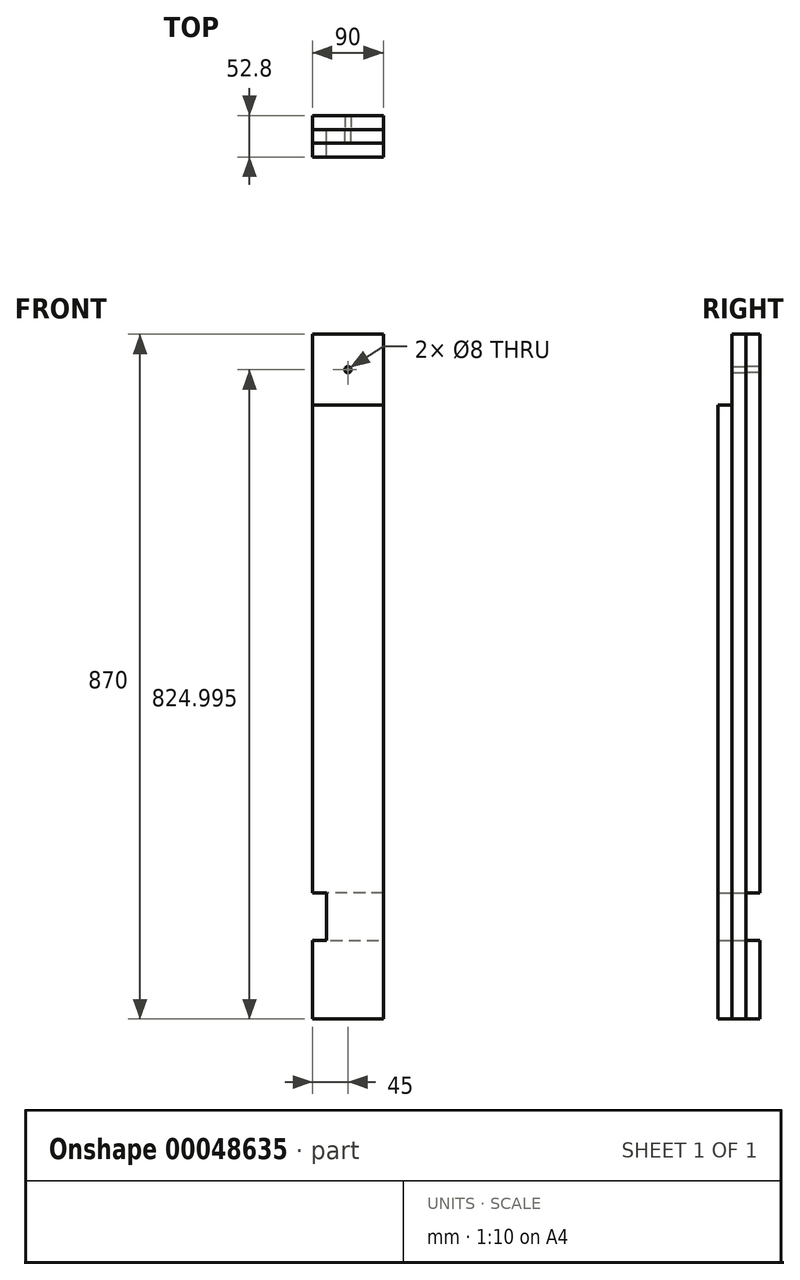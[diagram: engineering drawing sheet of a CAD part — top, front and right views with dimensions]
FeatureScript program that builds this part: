
annotation { "Feature Type Name" : "Feature", "Feature Type Description" : "" }
export const myFeature = defineFeature(function(context is Context, id is Id, definition is map)
    precondition{}
    {
        {
            assignVariable(context, id + "F0", {"name" : "mat1", "anyValue" : 17.6});
        }
        {
            var Q0;
            Q0=qCreatedBy(makeId("Front.planeOp"),FACE);
            var sketch = newSketch(context, id + "F1", { "sketchPlane" : qUnion([Q0])});
            skCircle(sketch, "E0.1", {"center": v(0, 211.88) * mm, "radius": 4 * mm});
            skLineSegment(sketch, "E0.2", {"start": v(-45, 256.87) * mm, "end": v(-45, -453.13) * mm});
            skLineSegment(sketch, "E0.3", {"start": v(45, 256.87) * mm, "end": v(45, -613.13) * mm});
            skLineSegment(sketch, "E1", {"start": v(-45, 256.87) * mm, "end": v(45, 256.87) * mm});
            skLineSegment(sketch, "E2", {"start": v(45, -613.13) * mm, "end": v(-45, -613.13) * mm});
            skPoint(sketch, "E3.orphan", {"position": v(45, 166.88) * mm});
            skPoint(sketch, "E4.orphan", {"position": v(-45, 166.87) * mm});
            skLineSegment(sketch, "E5.trimOffspring", {"start": v(-27.4, -453.13) * mm, "end": v(-27.4, -513.13) * mm});
            skLineSegment(sketch, "E6.trimOffspring", {"start": v(-27.4, -513.13) * mm, "end": v(-45, -513.13) * mm});
            skLineSegment(sketch, "E7.trimOffspring", {"start": v(-27.4, -453.13) * mm, "end": v(-45, -453.13) * mm});
            skLineSegment(sketch, "E8.trimOffspring", {"start": v(-45, -513.13) * mm, "end": v(-45, -613.13) * mm});
            skSolve(sketch);
        }
        {
            var Q0;
            Q0=makeQuery(id+"F1.imprint","IMPRINT",FACE,{"disambiguationData":[TD([[makeQuery(id+"F1.imprint","IMPRINT",EDGE,{"derivedFrom":sQuery(id+"F1.wireOp",EDGE,"E0.1")}),-1.0]])]});
            extrude(context, id + "F2", {"entities" : qUnion([Q0]), "depth" : (getVariable(context, 'mat1')) * mm});
        }
        {
            var Q0;
            Q0=makeQuery(id+"F2.opExtrude","CAP_FACE",FACE,{"disambiguationData":[OSD([sQuery(id+"F1.wireOp",EDGE,"E0.1"),sQuery(id+"F1.wireOp",EDGE,"E0.2"),sQuery(id+"F1.wireOp",EDGE,"E0.3"),sQuery(id+"F1.wireOp",EDGE,"E1"),sQuery(id+"F1.wireOp",EDGE,"E2")])],"isStart":false});
            var sketch = newSketch(context, id + "F3", { "sketchPlane" : qUnion([Q0])});
            skLineSegment(sketch, "E9.bottom", {"start": v(-45, 166.87) * mm, "end": v(45, 166.87) * mm});
            skLineSegment(sketch, "E9.top", {"start": v(-45, -613.13) * mm, "end": v(45, -613.13) * mm});
            skLineSegment(sketch, "E9.left", {"start": v(-45, 166.87) * mm, "end": v(-45, -453.13) * mm});
            skLineSegment(sketch, "E9.right", {"start": v(45, 166.87) * mm, "end": v(45, -613.13) * mm});
            skLineSegment(sketch, "E10.0.0", {"start": v(-45, 256.87) * mm, "end": v(45, 256.87) * mm});
            skLineSegment(sketch, "E10.0.1", {"start": v(45, 256.87) * mm, "end": v(45, -613.13) * mm});
            skLineSegment(sketch, "E10.0.2", {"start": v(45, -613.13) * mm, "end": v(-45, -613.13) * mm});
            skLineSegment(sketch, "E10.0.3", {"start": v(-45, -613.13) * mm, "end": v(-45, -513.13) * mm});
            skLineSegment(sketch, "E10.0.4", {"start": v(-45, -513.13) * mm, "end": v(-27.4, -513.13) * mm});
            skLineSegment(sketch, "E10.0.5", {"start": v(-27.4, -513.13) * mm, "end": v(-27.4, -453.13) * mm});
            skLineSegment(sketch, "E10.0.6", {"start": v(-27.4, -453.13) * mm, "end": v(-45, -453.13) * mm});
            skLineSegment(sketch, "E10.0.7", {"start": v(-45, -453.13) * mm, "end": v(-45, 256.87) * mm});
            skLineSegment(sketch, "E11.trimOffspring", {"start": v(-45, -513.13) * mm, "end": v(-45, -613.13) * mm});
            skSolve(sketch);
        }
        {
            var Q0;
            Q0=makeQuery(id+"F3.imprint","IMPRINT",FACE,{"disambiguationData":[TD([[makeQuery(id+"F3.imprint","IMPRINT",EDGE,{"derivedFrom":sQuery(id+"F3.wireOp",EDGE,"E9.bottom")}),-1.0]])]});
            extrude(context, id + "F4", {"entities" : qUnion([Q0]), "depth" : (getVariable(context, 'mat1')) * mm});
        }
        {
            var Q0;
            Q0=qCreatedBy(makeId("Front.planeOp"),FACE);
            var sketch = newSketch(context, id + "F5", { "sketchPlane" : qUnion([Q0])});
            skCircle(sketch, "E12.0", {"center": v(0, 211.88) * mm, "radius": 4 * mm});
            skLineSegment(sketch, "E12.1", {"start": v(-45, 256.87) * mm, "end": v(-45, -453.13) * mm});
            skLineSegment(sketch, "E12.2", {"start": v(-45, 256.87) * mm, "end": v(45, 256.87) * mm});
            skLineSegment(sketch, "E12.3", {"start": v(45, 256.87) * mm, "end": v(45, -453.13) * mm});
            skLineSegment(sketch, "E12.4", {"start": v(45, -613.13) * mm, "end": v(-45, -613.13) * mm});
            skLineSegment(sketch, "E12.5", {"start": v(-45, -513.13) * mm, "end": v(-45, -613.13) * mm});
            skLineSegment(sketch, "E12.6", {"start": v(-27.4, -513.13) * mm, "end": v(-45, -513.13) * mm});
            skLineSegment(sketch, "E12.8", {"start": v(-27.4, -453.13) * mm, "end": v(-45, -453.13) * mm});
            skLineSegment(sketch, "E13", {"start": v(-45, -453.13) * mm, "end": v(45, -453.13) * mm});
            skLineSegment(sketch, "E14", {"start": v(-45, -513.13) * mm, "end": v(45, -513.13) * mm});
            skLineSegment(sketch, "E15.trimOffspring", {"start": v(45, -513.13) * mm, "end": v(45, -613.13) * mm});
            skSolve(sketch);
        }
        {
            var Q0;
            Q0=makeQuery(id+"F5.imprint","IMPRINT",FACE,{"disambiguationData":[TD([[makeQuery(id+"F5.imprint","IMPRINT",EDGE,{"derivedFrom":sQuery(id+"F5.wireOp",EDGE,"E12.0")}),-1.0]])]});
            var Q1;
            Q1=makeQuery(id+"F5.imprint","IMPRINT",FACE,{"disambiguationData":[TD([[makeQuery(id+"F5.imprint","IMPRINT",EDGE,{"derivedFrom":sQuery(id+"F5.wireOp",EDGE,"E12.4")}),-1.0]])]});
            extrude(context, id + "F6", {"entities" : qUnion([Q0, Q1]), "oppositeDirection" : true, "depth" : (getVariable(context, 'mat1')) * mm});
        }
    });
